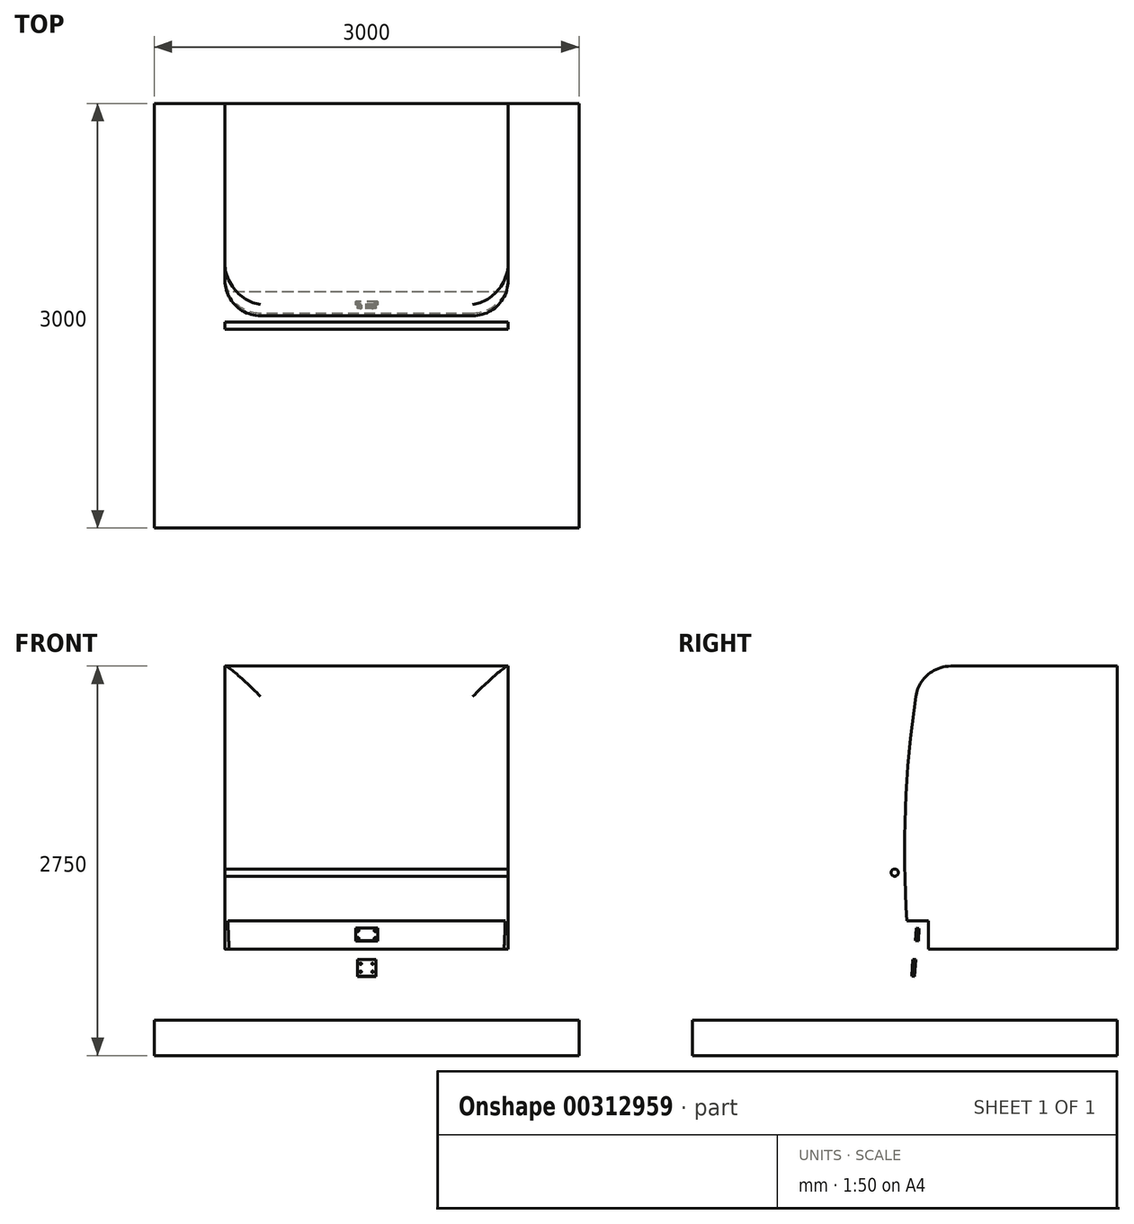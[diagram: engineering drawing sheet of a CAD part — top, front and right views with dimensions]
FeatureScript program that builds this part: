
annotation { "Feature Type Name" : "Feature", "Feature Type Description" : "" }
export const myFeature = defineFeature(function(context is Context, id is Id, definition is map)
    precondition{}
    {
        {
            var Q0;
            Q0=qCreatedBy(makeId("Right.planeOp"),FACE);
            var sketch = newSketch(context, id + "F0", { "sketchPlane" : qUnion([Q0])});
            skLineSegment(sketch, "E0.bottom", {"start": v(-1500, 0) * mm, "end": v(1500, 0) * mm});
            skLineSegment(sketch, "E0.top", {"start": v(-1500, -250) * mm, "end": v(1500, -250) * mm});
            skLineSegment(sketch, "E0.left", {"start": v(-1500, 0) * mm, "end": v(-1500, -250) * mm});
            skLineSegment(sketch, "E0.right", {"start": v(1500, 0) * mm, "end": v(1500, -250) * mm});
            skSolve(sketch);
        }
        {
            var Q0;
            Q0 = qSketchRegion(id + "F0", true);
            extrude(context, id + "F1", {"entities" : qUnion([Q0]), "depth" : 1500 * mm, "offsetDistance" : 25 * mm, "hasSecondDirection" : true, "secondDirectionOppositeDirection" : true, "secondDirectionDepth" : 1500 * mm});
        }
        {
            var Q0;
            Q0=qCreatedBy(makeId("Right.planeOp"),FACE);
            var sketch = newSketch(context, id + "F2", { "sketchPlane" : qUnion([Q0])});
            skLineSegment(sketch, "E1", {"start": v(50, 310) * mm, "end": v(58, 429.73) * mm});
            skLineSegment(sketch, "E2", {"start": v(58, 429.73) * mm, "end": v(77.96, 428.4) * mm});
            skLineSegment(sketch, "E3", {"start": v(77.96, 428.4) * mm, "end": v(69.96, 308.67) * mm});
            skLineSegment(sketch, "E4", {"start": v(69.96, 308.67) * mm, "end": v(50, 310) * mm});
            skSolve(sketch);
        }
        {
            var Q0;
            Q0 = qSketchRegion(id + "F2", true);
            extrude(context, id + "F3", {"entities" : qUnion([Q0]), "depth" : 65 * mm, "offsetDistance" : 25 * mm, "hasSecondDirection" : true, "secondDirectionOppositeDirection" : true, "secondDirectionDepth" : 65 * mm});
        }
        {
            var Q0;
            Q0=qCreatedBy(makeId("Right.planeOp"),FACE);
            var sketch = newSketch(context, id + "F4", { "sketchPlane" : qUnion([Q0])});
            skLineSegment(sketch, "E5", {"start": v(77, 560.2) * mm, "end": v(83, 650) * mm});
            skLineSegment(sketch, "E6", {"start": v(83, 650) * mm, "end": v(102.96, 648.67) * mm});
            skLineSegment(sketch, "E7", {"start": v(102.96, 648.67) * mm, "end": v(96.96, 558.87) * mm});
            skLineSegment(sketch, "E8", {"start": v(96.96, 558.87) * mm, "end": v(77, 560.2) * mm});
            skSolve(sketch);
        }
        {
            var Q0;
            Q0 = qSketchRegion(id + "F4", true);
            extrude(context, id + "F5", {"entities" : qUnion([Q0]), "depth" : 77.5 * mm, "offsetDistance" : 25 * mm, "hasSecondDirection" : true, "secondDirectionOppositeDirection" : true, "secondDirectionDepth" : 77.5 * mm});
        }
        {
            var Q0;
            Q0=qCreatedBy(makeId("Right.planeOp"),FACE);
            var sketch = newSketch(context, id + "F6", { "sketchPlane" : qUnion([Q0])});
            skCircle(sketch, "E9", {"center": v(-70, 1042) * mm, "radius": 25.5 * mm});
            skArc(sketch, "E10", {"start": v(113.53, 2500) * mm, "mid": v(10.83, 1602.92) * mm, "end": v(16.69, 700) * mm});
            skLineSegment(sketch, "E11", {"start": v(16.69, 700) * mm, "end": v(166.69, 700) * mm});
            skLineSegment(sketch, "E12", {"start": v(166.69, 700) * mm, "end": v(166.69, 500) * mm});
            skLineSegment(sketch, "E13", {"start": v(166.69, 500) * mm, "end": v(1500, 500) * mm});
            skLineSegment(sketch, "E14", {"start": v(1500, 500) * mm, "end": v(1500, 2500) * mm});
            skLineSegment(sketch, "E15", {"start": v(1500, 2500) * mm, "end": v(113.53, 2500) * mm});
            skSolve(sketch);
        }
        {
            var Q0;
            Q0 = qSketchRegion(id + "F6", true);
            extrude(context, id + "F7", {"entities" : qUnion([Q0]), "depth" : 1000 * mm, "offsetDistance" : 25 * mm, "hasSecondDirection" : true, "secondDirectionOppositeDirection" : true, "secondDirectionDepth" : 1000 * mm});
        }
        {
            var Q0;
            Q0=makeQuery(id+"F7.opExtrude","CAP_EDGE",EDGE,{"disambiguationData":[OSD([sQuery(id+"F6.wireOp",EDGE,"E10")])],"isStart":true});
            var Q1;
            Q1=makeQuery(id+"F7.opExtrude","CAP_EDGE",EDGE,{"disambiguationData":[OSD([sQuery(id+"F6.wireOp",EDGE,"E10")])],"isStart":false});
            var Q2;
            Q2=makeQuery(id+"F7.opExtrude","SWEPT_EDGE",EDGE,{"disambiguationData":[OSD([sQuery(id+"F6.wireOp",EDGE,"E10"),sQuery(id+"F6.wireOp",EDGE,"E15")])]});
            fillet(context, id + "F8", {"entities" : qUnion([Q0, Q1, Q2]), "radius" : 250 * mm, "tangentPropagation" : true, "allowEdgeOverflow" : false});
        }
        {
            var Q0;
            Q0=makeQuery(id+"F5.opExtrude","SWEPT_FACE",FACE,{"disambiguationData":[OSD([sQuery(id+"F4.wireOp",EDGE,"E5")])]});
            var sketch = newSketch(context, id + "F9", { "sketchPlane" : qUnion([Q0])});
            skLineSegment(sketch, "E16.bottom", {"start": v(-61, 636.59) * mm, "end": v(61, 636.59) * mm});
            skLineSegment(sketch, "E16.top", {"start": v(-61, 581.59) * mm, "end": v(61, 581.59) * mm});
            skLineSegment(sketch, "E16.left", {"start": v(-61, 636.59) * mm, "end": v(-61, 581.59) * mm});
            skLineSegment(sketch, "E16.right", {"start": v(61, 636.59) * mm, "end": v(61, 581.59) * mm});
            skLineSegment(sketch, "E17", {"start": v(77.5, 609.09) * mm, "end": v(61, 609.09) * mm});
            skLineSegment(sketch, "E18", {"start": v(0, 654.09) * mm, "end": v(0, 636.59) * mm});
            skSolve(sketch);
        }
        {
            var Q0;
            Q0=sQuery(id+"F9.wireOp",VERTEX,"E16.bottom.start");
            var Q1;
            Q1=sQuery(id+"F9.wireOp",VERTEX,"E16.right.start");
            var Q2;
            Q2=sQuery(id+"F9.wireOp",VERTEX,"E16.right.end");
            var Q3;
            Q3=sQuery(id+"F9.wireOp",VERTEX,"E16.left.end");
            var Q4;
            Q4=makeQuery(id+"F5.opExtrude","SWEPT_BODY",BODY,{"disambiguationData":[OSD([sQuery(id+"F4.wireOp",EDGE,"E5"),sQuery(id+"F4.wireOp",EDGE,"E6"),sQuery(id+"F4.wireOp",EDGE,"E7"),sQuery(id+"F4.wireOp",EDGE,"E8")])]});
            hole(context, id + "F10", {"style" : HoleStyle.SIMPLE, "endStyle" : HoleEndStyle.THROUGH, "holeDiameter" : 14 * mm, "isTappedThrough" : true, "tappedDepth" : 12 * mm, "tapClearance" : 3, "locations" : qUnion([Q0, Q1, Q2, Q3]), "scope" : qUnion([Q4])});
        }
        {
            var Q0;
            Q0=makeQuery(id+"F3.opExtrude","SWEPT_FACE",FACE,{"disambiguationData":[OSD([sQuery(id+"F2.wireOp",EDGE,"E1")])]});
            var sketch = newSketch(context, id + "F11", { "sketchPlane" : qUnion([Q0])});
            skLineSegment(sketch, "E19.bottom", {"start": v(-42, 401.14) * mm, "end": v(42, 401.14) * mm});
            skLineSegment(sketch, "E19.top", {"start": v(-42, 344.14) * mm, "end": v(42, 344.14) * mm});
            skLineSegment(sketch, "E19.left", {"start": v(-42, 401.14) * mm, "end": v(-42, 344.14) * mm});
            skLineSegment(sketch, "E19.right", {"start": v(42, 401.14) * mm, "end": v(42, 344.14) * mm});
            skLineSegment(sketch, "E20", {"start": v(0, 401.14) * mm, "end": v(0, 432.64) * mm});
            skLineSegment(sketch, "E21", {"start": v(42, 372.64) * mm, "end": v(65, 372.64) * mm});
            skSolve(sketch);
        }
        {
            var Q0;
            Q0=sQuery(id+"F11.wireOp",VERTEX,"E19.bottom.start");
            var Q1;
            Q1=sQuery(id+"F11.wireOp",VERTEX,"E19.right.end");
            var Q2;
            Q2=sQuery(id+"F11.wireOp",VERTEX,"E19.left.end");
            var Q3;
            Q3=sQuery(id+"F11.wireOp",VERTEX,"E19.right.start");
            var Q4;
            Q4=makeQuery(id+"F3.opExtrude","SWEPT_BODY",BODY,{"disambiguationData":[OSD([sQuery(id+"F2.wireOp",EDGE,"E1"),sQuery(id+"F2.wireOp",EDGE,"E2"),sQuery(id+"F2.wireOp",EDGE,"E3"),sQuery(id+"F2.wireOp",EDGE,"E4")])]});
            hole(context, id + "F12", {"style" : HoleStyle.SIMPLE, "endStyle" : HoleEndStyle.THROUGH, "holeDiameter" : 12 * mm, "isTappedThrough" : true, "tappedDepth" : 12 * mm, "tapClearance" : 3, "locations" : qUnion([Q0, Q1, Q2, Q3]), "scope" : qUnion([Q4])});
        }
    });
